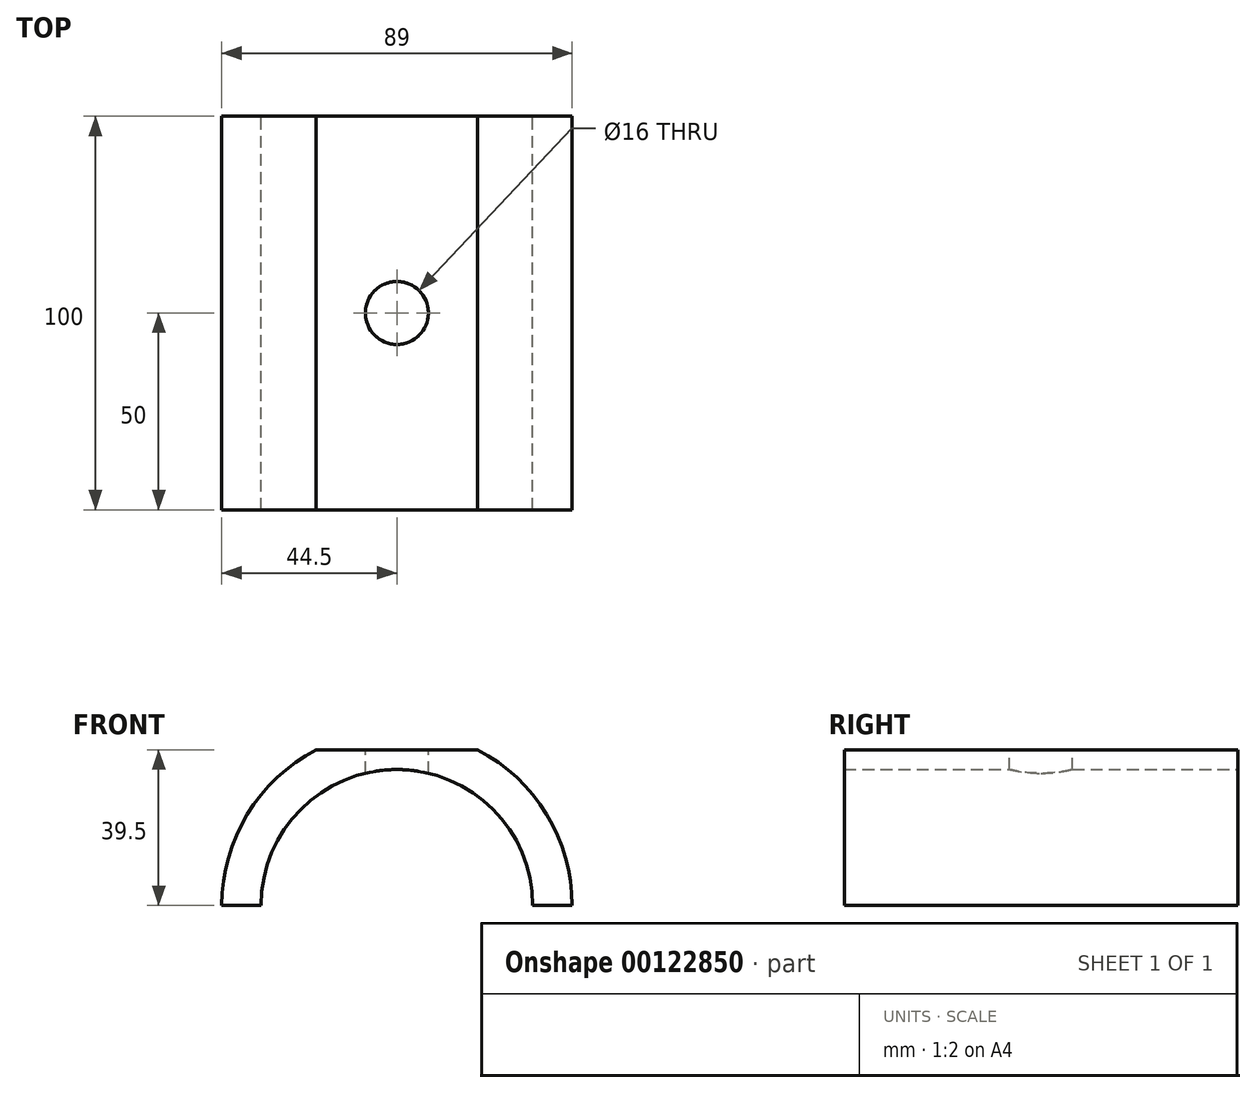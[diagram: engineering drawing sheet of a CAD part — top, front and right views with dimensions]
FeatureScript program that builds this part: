
annotation { "Feature Type Name" : "Feature", "Feature Type Description" : "" }
export const myFeature = defineFeature(function(context is Context, id is Id, definition is map)
    precondition{}
    {
        {
            var Q0;
            Q0=qCreatedBy(makeId("Front.planeOp"),FACE);
            var sketch = newSketch(context, id + "F0", { "sketchPlane" : qUnion([Q0])});
            skArc(sketch, "E0", {"start": v(44.5, 0) * mm, "mid": v(38.03, 23.11) * mm, "end": v(20.5, 39.5) * mm});
            skArc(sketch, "E1", {"start": v(34.5, 0) * mm, "mid": v(0, 34.5) * mm, "end": v(-34.5, 0) * mm});
            skLineSegment(sketch, "E2", {"start": v(-20.5, 39.5) * mm, "end": v(20.5, 39.5) * mm});
            skLineSegment(sketch, "E3", {"start": v(-44.5, 0) * mm, "end": v(-34.5, 0) * mm});
            skLineSegment(sketch, "E4.trimOffspring", {"start": v(34.5, 0) * mm, "end": v(44.5, 0) * mm});
            skArc(sketch, "E5.trimOffspring", {"start": v(-20.5, 39.5) * mm, "mid": v(-38.03, 23.11) * mm, "end": v(-44.5, 0) * mm});
            skSolve(sketch);
        }
        {
            var Q0;
            Q0 = qSketchRegion(id + "F0", true);
            extrude(context, id + "F1", {"entities" : qUnion([Q0]), "depth" : 100 * mm});
        }
        {
            var Q0;
            Q0=makeQuery(id+"F1.opExtrude","SWEPT_FACE",FACE,{"disambiguationData":[OSD([sQuery(id+"F0.wireOp",EDGE,"E2")])]});
            var sketch = newSketch(context, id + "F2", { "sketchPlane" : qUnion([Q0])});
            skPoint(sketch, "E6", {"position": v(0, -50) * mm});
            skSolve(sketch);
        }
        {
            var Q0;
            Q0=sQuery(id+"F2.wireOp",VERTEX,"E6");
            var Q1;
            Q1=makeQuery(id+"F1.opExtrude","SWEPT_BODY",BODY,{"disambiguationData":[OSD([sQuery(id+"F0.wireOp",EDGE,"E0"),sQuery(id+"F0.wireOp",EDGE,"E1"),sQuery(id+"F0.wireOp",EDGE,"E2"),sQuery(id+"F0.wireOp",EDGE,"E3"),sQuery(id+"F0.wireOp",EDGE,"E4.trimOffspring"),sQuery(id+"F0.wireOp",EDGE,"E5.trimOffspring")])]});
            hole(context, id + "F3", {"style" : HoleStyle.SIMPLE, "endStyle" : HoleEndStyle.THROUGH, "holeDiameter" : 16 * mm, "locations" : qUnion([Q0]), "scope" : qUnion([Q1]), "isTappedThrough" : true});
        }
    });
